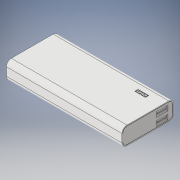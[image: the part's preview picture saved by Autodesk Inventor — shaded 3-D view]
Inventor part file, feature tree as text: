
AUTODESK INVENTOR PART (.ipt)
format: ipt  version: 2018 (Build 220112000, 112)  size: 273,408 bytes
history: native  units: in
note: dims shown in document units (in); Inventor stores cm internally (conversion verified against a paired STEP export)
features: extrude x6, sketch x6, fillet x1, mirror x1, projected_geometry x1
ambient origin geometry x8: Origin, YZ Plane, XZ Plane, XY Plane, X Axis, Y Axis, Z Axis, Center Point
bodies: Solid1 (feature_tree)
feature tree (15):
  extrude  "Extrusion1"  Depth=2.4803in
  fillet  "Fillet1"  Radius=5.5512in
  extrude  "Extrusion2"  Depth=0.5512in
  extrude  "Extrusion3"  Depth=0.2756in
  extrude  "Extrusion4"  Depth=0.0472in
  extrude  "Extrusion5"  Depth=0.0453in
  extrude  "Extrusion6"  Depth=0.3937in TaperAngle=0.0deg
  mirror  "Mirror1"
  sketch  "Sketch1"  dims[d0=0.8661in d1=2.4803in d2=5.5512in d3=0.0in]
  sketch  "Sketch2"  dims[d4=0.2362in d5=0.5512in]
  sketch  "Sketch3"  dims[d6=0.2362in d7=0.2756in]
  sketch  "Sketch4"  dims[d8=0.1575in d12=0.0472in]
  sketch  "Sketch5"  dims[d13=0.0472in d14=0.0453in]
  sketch  "Sketch6"  dims[d15=0.1417in d16=0.5512in d17=0.2362in d18=0.0472in d19=0.0472in d20=0.0453in d21=0.1417in d22=0.1378in d23=0.3937in d24=0.0in d25=0.5118in d26=0.1575in d27=0.0787in d28=0.1181in d29=0.0197in d30=0.0197in d31=1.5748in d33=0.1299in d34=0.3937in d36=0.3937in d38=0.0098in d39=0.0in d42=0.1181in d43=1.378in d44=0.2756in d45=0.0787in d46=0.2749in d47=0.1969in d48=0.0in d49=0.5512in d50=0.315in d51=0.0098in d52=0.315in d53=0.0039in d54=0.0in d55=0.0394in d56=0.0492in d57=0.0039in d58=0.0in]
  projected_geometry  "Projected Loop1"
